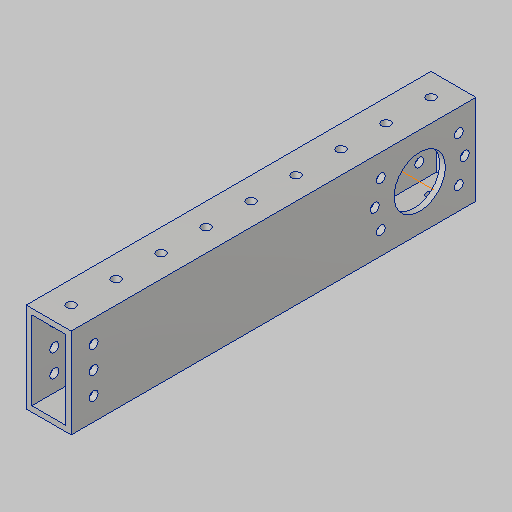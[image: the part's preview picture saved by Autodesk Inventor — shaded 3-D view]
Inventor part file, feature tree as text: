
AUTODESK INVENTOR PART (.ipt)
format: ipt  version: 2023.5 (Build 275446000, 446)  size: 274,432 bytes
history: native  units: in
note: dims shown in document units (in); Inventor stores cm internally (conversion verified against a paired STEP export)
features: sketch x6, hole x5, projected_geometry x5, extrude x4, pattern_linear x1, other x1
ambient origin geometry x8: Origin, YZ Plane, XZ Plane, XY Plane, X Axis, Y Axis, Z Axis, Center Point
bodies: Solid1 (feature_tree)
feature tree (22):
  extrude  "Extrusion1"  Depth=1.125in
  extrude  "Extrusion3"  TaperAngle=0.0deg  [1 undecoded]
  extrude  "Extrusion4"  TaperAngle=45.0deg  [1 undecoded]
  hole  "Hole1"  [1 undecoded]
  pattern_linear  "Rectangular Pattern1"  Spacing1=0.0in  [1 undecoded]
  extrude  "Extrusion5"  Depth=1.0in
  hole  "Hole2"  [1 undecoded]
  sketch  "Sketch8"  dims[d29=45.0deg d30=0.0in d31=0.0in d32=0.5in d33=0.5in d34=0.5in d35=0.201in d36=0.75in d37=0.375in d38=0.25in d39=0.5635in d40=1.0in d41=0.8108in d42=1.875in d43=2.0in d44=4.0in d45=6.0in d46=1.25in d47=2.3622in d49=360.0deg d51=4.7244in d53=360.0deg d55=0.177in d56=0.75in d57=0.332in d58=0.25in d59=0.5635in d60=1.0in d61=0.8108in d62=0.201in d63=0.75in d64=0.385in d65=0.25in d66=0.5635in d67=1.0in d68=0.8108in d69=1.14in d70=0.75in d71=0.375in d72=0.25in d73=0.5635in d74=1.0in d75=0.8108in]
  hole  "Hole3"  [1 undecoded]
  hole  "Hole4"  [1 undecoded]
  hole  "Hole5"  [1 undecoded]
  other  "Work Axis1"
  sketch  "Sketch3"  dims[d4=0.0in d8=1.125in]
  sketch  "Sketch4"  dims[d9=1.0in d10=0.0in d11=0.0in]
  projected_geometry  "Projected Loop2"
  sketch  "Sketch5"  dims[d14=0.0in d15=0.0in d17=45.0deg]
  sketch  "Sketch6"  dims[d18=0.5in]
  sketch  "Sketch7"  dims[d19=0.201in d20=0.75in d21=0.385in d22=0.25in d23=0.5635in d24=1.0in d25=0.8108in d26=3.5433in d28=1.0in]
  projected_geometry  "Project Cut Edges1"
  projected_geometry  "Project Cut Edges2"
  projected_geometry  "Project Cut Edges3"
  projected_geometry  "Project Cut Edges4"
note: 8 required parameter values undecoded (feature->parameter linkage not recoverable at this tier; creation-order binding heuristic only, values carry confidence <= 0.55)
